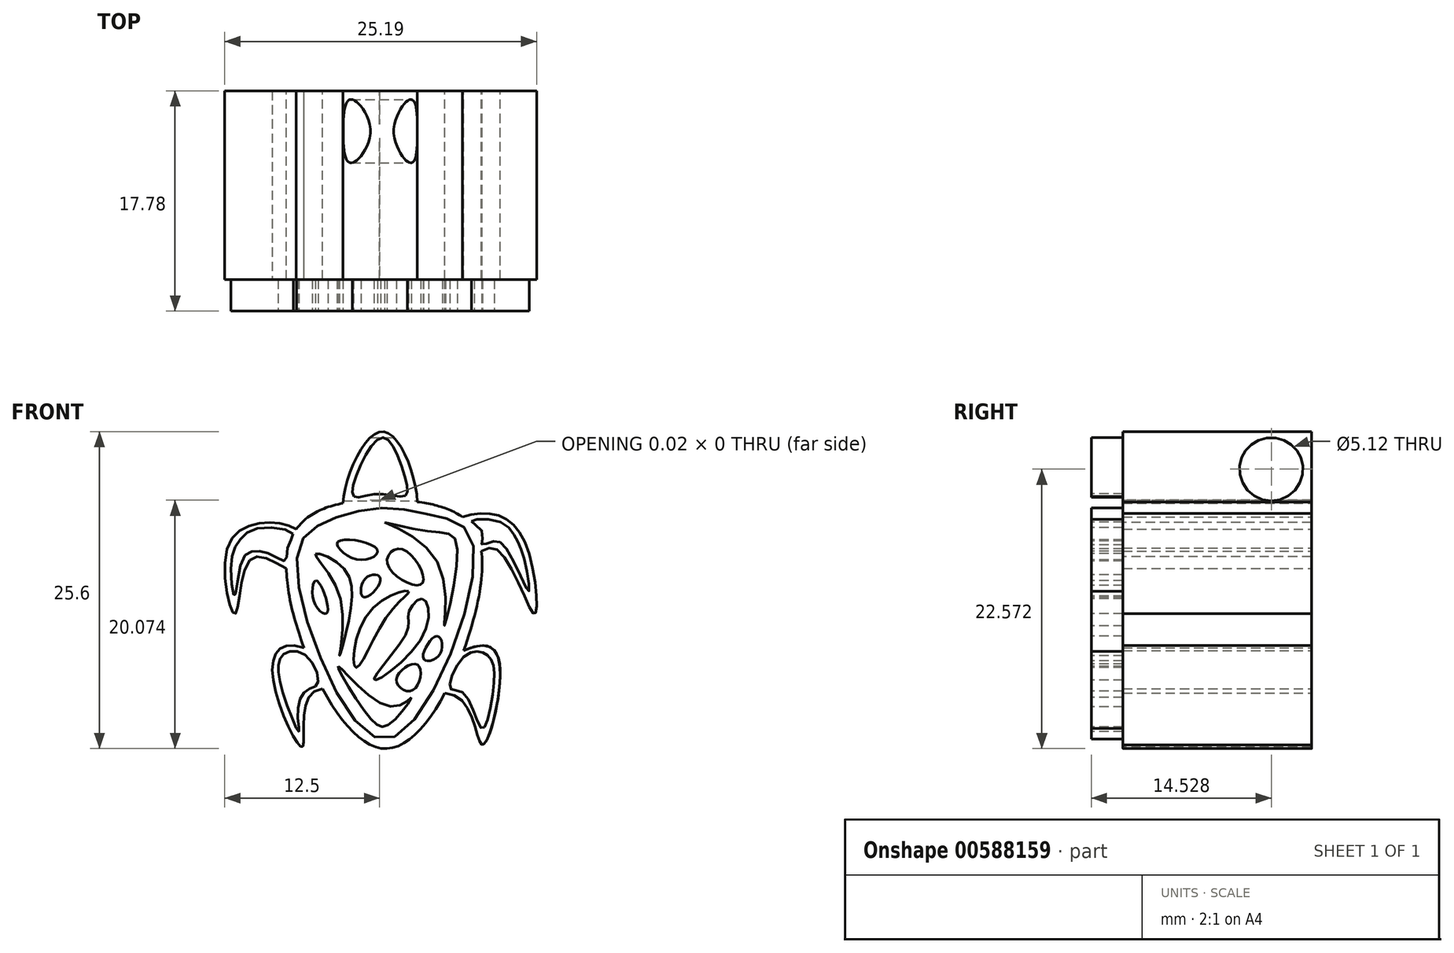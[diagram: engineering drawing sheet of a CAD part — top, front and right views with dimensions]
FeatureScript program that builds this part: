
annotation { "Feature Type Name" : "Feature", "Feature Type Description" : "" }
export const myFeature = defineFeature(function(context is Context, id is Id, definition is map)
    precondition{}
    {
        {
            var Q0;
            Q0=qCreatedBy(makeId("Front.planeOp"),FACE);
            var sketch = newSketch(context, id + "F0", { "sketchPlane" : qUnion([Q0])});
            skLineSegment(sketch, "E0.bottom", {"start": v(-20.81, 14.8) * mm, "end": v(4.78, 14.8) * mm});
            skLineSegment(sketch, "E0.top", {"start": v(-20.81, -10.8) * mm, "end": v(4.78, -10.8) * mm});
            skLineSegment(sketch, "E0.left", {"start": v(-20.81, 14.8) * mm, "end": v(-20.81, -10.8) * mm});
            skLineSegment(sketch, "E0.right", {"start": v(4.78, 14.8) * mm, "end": v(4.78, -10.8) * mm});
            skSolve(sketch);
        }
        {
            var Q0;
            Q0=qCreatedBy(makeId("Front.planeOp"),FACE);
            var sketch = newSketch(context, id + "F1", { "sketchPlane" : qUnion([Q0])});
            skFitSpline(sketch, "E1", {"points": [v(-7.9, 9.17) * mm, v(-2.14, 8.16) * mm, v(0, 3.25) * mm, v(-7.72, -10.9) * mm, v(-15.76, 2.93) * mm, v(-13.47, 8.16) * mm, v(-7.9, 9.17) * mm]});
            skSolve(sketch);
        }
        {
            var Q0;
            Q0 = qSketchRegion(id + "F1", true);
            extrude(context, id + "F2", {"entities" : qUnion([Q0]), "depth" : 25.4 * mm, "offsetDistance" : 25.4 * mm});
        }
        {
            var Q0;
            Q0=qCreatedBy(makeId("Front.planeOp"),FACE);
            var sketch = newSketch(context, id + "F3", { "sketchPlane" : qUnion([Q0])});
            skFitSpline(sketch, "E2", {"points": [v(-8.27, 9.17) * mm, v(-9, 7.94) * mm, v(-11.07, 7.83) * mm, v(-8.02, 14.7) * mm, v(-5.4, 7.61) * mm, v(-7.48, 7.83) * mm, v(-8.27, 9.17) * mm]});
            skSolve(sketch);
        }
        {
            var Q0;
            Q0 = qSketchRegion(id + "F3", true);
            extrude(context, id + "F4", {"entities" : qUnion([Q0]), "operationType" : NewBodyOperationType.ADD, "depth" : 25.4 * mm, "offsetDistance" : 25.4 * mm});
        }
        {
            var Q0;
            Q0=qCreatedBy(makeId("Front.planeOp"),FACE);
            var sketch = newSketch(context, id + "F5", { "sketchPlane" : qUnion([Q0])});
            skFitSpline(sketch, "E3", {"points": [v(-2.31, 7.52) * mm, v(1.17, 7.98) * mm, v(3.83, 4.78) * mm, v(4.2, 0) * mm, v(1.08, 5.23) * mm, v(-1.67, 4.23) * mm, v(-3.32, 6.15) * mm, v(-2.31, 7.52) * mm]});
            skFitSpline(sketch, "E4", {"points": [v(-14.23, 5.87) * mm, v(-16.8, 7.34) * mm, v(-20.55, 5.33) * mm, v(-19.91, 0) * mm, v(-18.54, 4.5) * mm, v(-14.78, 3.4) * mm, v(-14.23, 5.87) * mm]});
            skSolve(sketch);
        }
        {
            var Q0;
            Q0 = qSketchRegion(id + "F5", true);
            extrude(context, id + "F6", {"entities" : qUnion([Q0]), "operationType" : NewBodyOperationType.ADD, "depth" : 25.4 * mm, "offsetDistance" : 25.4 * mm});
        }
        {
            var Q0;
            Q0=makeQuery(id+"F0.imprint","IMPRINT",FACE,{"disambiguationData":[TD([[makeQuery(id+"F0.imprint","IMPRINT",EDGE,{"derivedFrom":sQuery(id+"F0.wireOp",EDGE,"E0.bottom")}),-1.0]])]});
            var sketch = newSketch(context, id + "F7", { "sketchPlane" : qUnion([Q0])});
            skFitSpline(sketch, "E5", {"points": [v(-15.18, -2.57) * mm, v(-16.88, -5.2) * mm, v(-14.5, -10.74) * mm, v(-13.72, -6.43) * mm, v(-9.79, -6.04) * mm, v(-15.18, -2.57) * mm]});
            skFitSpline(sketch, "E6", {"points": [v(0, -2.57) * mm, v(1.44, -5.72) * mm, v(0, -10.59) * mm, v(-1.9, -6.8) * mm, v(-5.65, -6.16) * mm, v(0, -2.57) * mm]});
            skSolve(sketch);
        }
        {
            var Q0;
            Q0 = qSketchRegion(id + "F7", true);
            extrude(context, id + "F8", {"entities" : qUnion([Q0]), "operationType" : NewBodyOperationType.ADD, "depth" : 25.4 * mm, "offsetDistance" : 25.4 * mm});
        }
        {
            var Q0;
            Q0=makeQuery(id+"F8.boolean.opBoolean","MERGE",FACE,{"derivedFrom":[makeQuery(id+"F6.boolean.opBoolean","MERGE",FACE,{"derivedFrom":[makeQuery(id+"F4.boolean.opBoolean","MERGE",FACE,{"derivedFrom":[makeQuery(id+"F2.opExtrude","CAP_FACE",FACE,{"disambiguationData":[OSD([sQuery(id+"F1.wireOp",EDGE,"E1")])],"isStart":false}),makeQuery(id+"F4.opExtrude","CAP_FACE",FACE,{"disambiguationData":[OSD([sQuery(id+"F3.wireOp",EDGE,"E2")])],"isStart":false})]}),makeQuery(id+"F6.opExtrude","CAP_FACE",FACE,{"disambiguationData":[OSD([sQuery(id+"F5.wireOp",EDGE,"E3")])],"isStart":false}),makeQuery(id+"F6.opExtrude","CAP_FACE",FACE,{"disambiguationData":[OSD([sQuery(id+"F5.wireOp",EDGE,"E4")])],"isStart":false})]}),makeQuery(id+"F8.opExtrude","CAP_FACE",FACE,{"disambiguationData":[OSD([sQuery(id+"F7.wireOp",EDGE,"E5")])],"isStart":false}),makeQuery(id+"F8.opExtrude","CAP_FACE",FACE,{"disambiguationData":[OSD([sQuery(id+"F7.wireOp",EDGE,"E6")])],"isStart":false})]});
            extrude(context, id + "F9", {"entities" : qUnion([Q0]), "operationType" : NewBodyOperationType.REMOVE, "oppositeDirection" : true, "depth" : 10.16 * mm, "offsetDistance" : 25.4 * mm});
        }
        {
            var Q0;
            Q0=makeQuery(id+"F0.imprint","IMPRINT",FACE,{"disambiguationData":[TD([[makeQuery(id+"F0.imprint","IMPRINT",EDGE,{"derivedFrom":sQuery(id+"F0.wireOp",EDGE,"E0.bottom")}),-1.0]])]});
            var sketch = newSketch(context, id + "F10", { "sketchPlane" : qUnion([Q0])});
            skFitSpline(sketch, "E7", {"points": [v(-8.1, 8.53) * mm, v(-12.56, 7.45) * mm, v(-14.8, 5.3) * mm, v(-12.87, -3.96) * mm, v(-8.02, -10.13) * mm, v(-3.08, -4.5) * mm, v(-0.92, 6.3) * mm, v(-3.78, 7.91) * mm, v(-8.1, 8.53) * mm]});
            skSolve(sketch);
        }
        {
            var Q0;
            Q0 = qSketchRegion(id + "F10", true);
            extrude(context, id + "F11", {"entities" : qUnion([Q0]), "operationType" : NewBodyOperationType.ADD, "depth" : 17.78 * mm, "offsetDistance" : 25.4 * mm});
        }
        {
            var Q0;
            Q0=makeQuery(id+"F0.imprint","IMPRINT",FACE,{"disambiguationData":[TD([[makeQuery(id+"F0.imprint","IMPRINT",EDGE,{"derivedFrom":sQuery(id+"F0.wireOp",EDGE,"E0.bottom")}),-1.0]])]});
            var sketch = newSketch(context, id + "F12", { "sketchPlane" : qUnion([Q0])});
            skFitSpline(sketch, "E8", {"points": [v(-10.33, 9.45) * mm, v(-8.4, 9.68) * mm, v(-6.17, 9.53) * mm, v(-6.4, 11.61) * mm, v(-7.94, 14.23) * mm, v(-9.87, 11.84) * mm, v(-10.33, 9.45) * mm]});
            skSolve(sketch);
        }
        {
            var Q0;
            Q0 = qSketchRegion(id + "F12", true);
            extrude(context, id + "F13", {"entities" : qUnion([Q0]), "operationType" : NewBodyOperationType.ADD, "depth" : 17.78 * mm, "offsetDistance" : 25.4 * mm});
        }
        {
            var Q0;
            Q0=makeQuery(id+"F0.imprint","IMPRINT",FACE,{"disambiguationData":[TD([[makeQuery(id+"F0.imprint","IMPRINT",EDGE,{"derivedFrom":sQuery(id+"F0.wireOp",EDGE,"E0.bottom")}),-1.0]])]});
            var sketch = newSketch(context, id + "F14", { "sketchPlane" : qUnion([Q0])});
            skFitSpline(sketch, "E9", {"points": [v(-15.26, 6.45) * mm, v(-15.65, 5.52) * mm, v(-15.88, 4.29) * mm, v(-16.96, 4.75) * mm, v(-18.35, 5.06) * mm, v(-19.35, 4.37) * mm, v(-19.96, 1.44) * mm, v(-20.27, 3.83) * mm, v(-19.66, 5.83) * mm, v(-18.04, 6.9) * mm, v(-15.26, 6.45) * mm]});
            skSolve(sketch);
        }
        {
            var Q0;
            Q0 = qSketchRegion(id + "F14", true);
            extrude(context, id + "F15", {"entities" : qUnion([Q0]), "operationType" : NewBodyOperationType.ADD, "depth" : 17.78 * mm, "offsetDistance" : 25.4 * mm});
        }
        {
            var Q0;
            Q0=makeQuery(id+"F0.imprint","IMPRINT",FACE,{"disambiguationData":[TD([[makeQuery(id+"F0.imprint","IMPRINT",EDGE,{"derivedFrom":sQuery(id+"F0.wireOp",EDGE,"E0.bottom")}),-1.0]])]});
            var sketch = newSketch(context, id + "F16", { "sketchPlane" : qUnion([Q0])});
            skFitSpline(sketch, "E10", {"points": [v(-0.85, 7.45) * mm, v(0, 6.68) * mm, v(0, 5.6) * mm, v(0.85, 5.83) * mm, v(2, 5.21) * mm, v(3.78, 1.82) * mm, v(3.47, 4.21) * mm, v(2.77, 6.06) * mm, v(1.39, 7.45) * mm, v(-0.85, 7.45) * mm]});
            skFitSpline(sketch, "E11", {"points": [v(-14.26, -3.34) * mm, v(-13.26, -5.65) * mm, v(-14.18, -6.2) * mm, v(-14.88, -7.97) * mm, v(-14.8, -9.5) * mm, v(-16.03, -6.5) * mm, v(-16.42, -4.04) * mm, v(-15.88, -3.19) * mm, v(-14.26, -3.34) * mm]});
            skSolve(sketch);
        }
        {
            var Q0;
            Q0 = qSketchRegion(id + "F16", true);
            extrude(context, id + "F17", {"entities" : qUnion([Q0]), "operationType" : NewBodyOperationType.ADD, "depth" : 17.78 * mm, "offsetDistance" : 25.4 * mm});
        }
        {
            var Q0;
            Q0=makeQuery(id+"F0.imprint","IMPRINT",FACE,{"disambiguationData":[TD([[makeQuery(id+"F0.imprint","IMPRINT",EDGE,{"derivedFrom":sQuery(id+"F0.wireOp",EDGE,"E0.bottom")}),-1.0]])]});
            var sketch = newSketch(context, id + "F18", { "sketchPlane" : qUnion([Q0])});
            skFitSpline(sketch, "E12", {"points": [v(-1.46, -3.5) * mm, v(-2.54, -6.04) * mm, v(-1.46, -6.43) * mm, v(0, -9.28) * mm, v(0.92, -6.12) * mm, v(0.77, -3.73) * mm, v(0, -3.11) * mm, v(-1.46, -3.5) * mm]});
            skSolve(sketch);
        }
        {
            var Q0;
            Q0 = qSketchRegion(id + "F18", true);
            extrude(context, id + "F19", {"entities" : qUnion([Q0]), "operationType" : NewBodyOperationType.ADD, "depth" : 17.78 * mm, "offsetDistance" : 25.4 * mm});
        }
        {
            var Q0;
            Q0=qCreatedBy(makeId("Right.planeOp"),FACE);
            var sketch = newSketch(context, id + "F20", { "sketchPlane" : qUnion([Q0])});
            skCircle(sketch, "E13", {"center": v(-3.25, 11.67) * mm, "radius": 2.56 * mm});
            skSolve(sketch);
        }
        {
            var Q0;
            Q0 = qSketchRegion(id + "F20", true);
            extrude(context, id + "F21", {"entities" : qUnion([Q0]), "operationType" : NewBodyOperationType.REMOVE, "oppositeDirection" : true, "depth" : 25.4 * mm, "offsetDistance" : 25.4 * mm});
        }
        {
            var Q0;
            Q0=qCreatedBy(makeId("Front.planeOp"),FACE);
            var sketch = newSketch(context, id + "F22", { "sketchPlane" : qUnion([Q0])});
            skFitSpline(sketch, "E14", {"points": [v(-5.65, -1.95) * mm, v(-3.76, 0.96) * mm, v(-3.6, 3.35) * mm, v(-2.74, 2.24) * mm, v(-2.65, 0) * mm, v(-1.88, 2.24) * mm, v(-3.08, 4.21) * mm, v(-1.54, 3.78) * mm, v(-0.94, 2.58) * mm, v(-0.77, 4.13) * mm, v(-3.5, 5.4) * mm, v(-4.28, 6.86) * mm, v(-5.82, 7.3) * mm, v(-4.88, 6.35) * mm, v(-4.53, 4.98) * mm, v(-5.48, 5.75) * mm, v(-6.59, 5.67) * mm, v(-5.73, 5.24) * mm, v(-4.7, 3.95) * mm, v(-5.99, 4.13) * mm, v(-7.36, 2.84) * mm, v(-6.25, 3.18) * mm, v(-4.88, 3.18) * mm, v(-4.88, 0.87) * mm, v(-7.36, -1.95) * mm, v(-6.76, -2.3) * mm, v(-5.65, -1.95) * mm]});
            skSolve(sketch);
        }
        {
            var Q0;
            Q0 = qSketchRegion(id + "F22", true);
            extrude(context, id + "F23", {"entities" : qUnion([Q0]), "operationType" : NewBodyOperationType.ADD, "depth" : 2.54 * mm, "offsetDistance" : 25.4 * mm});
        }
        {
            var Q0;
            Q0=makeQuery(id+"F11.opExtrude","CAP_FACE",FACE,{"disambiguationData":[OSD([sQuery(id+"F10.wireOp",EDGE,"E7")])],"isStart":false});
            var sketch = newSketch(context, id + "F24", { "sketchPlane" : qUnion([Q0])});
            skFitSpline(sketch, "E15", {"points": [v(-8.2, 2.85) * mm, v(-9.41, 2.85) * mm, v(-9.52, 1.33) * mm, v(-8.2, 2.85) * mm]});
            skSolve(sketch);
        }
        {
            var Q0;
            Q0 = qSketchRegion(id + "F24", true);
            extrude(context, id + "F25", {"entities" : qUnion([Q0]), "operationType" : NewBodyOperationType.REMOVE, "oppositeDirection" : true, "depth" : 2.54 * mm, "offsetDistance" : 25.4 * mm});
        }
        {
            var Q0;
            Q0=makeQuery(id+"F11.opExtrude","CAP_FACE",FACE,{"disambiguationData":[OSD([sQuery(id+"F10.wireOp",EDGE,"E7")])],"isStart":false});
            var sketch = newSketch(context, id + "F26", { "sketchPlane" : qUnion([Q0])});
            skFitSpline(sketch, "E16", {"points": [v(-7.87, 7.38) * mm, v(-4.24, 6.66) * mm, v(-2.06, 5.69) * mm, v(-3.03, -0.97) * mm, v(-3.63, 4.24) * mm, v(-7.87, 7.38) * mm]});
            skSolve(sketch);
        }
        {
            var Q0;
            Q0 = qSketchRegion(id + "F26", true);
            extrude(context, id + "F27", {"entities" : qUnion([Q0]), "operationType" : NewBodyOperationType.REMOVE, "oppositeDirection" : true, "depth" : 2.54 * mm, "offsetDistance" : 25.4 * mm});
        }
        {
            var Q0;
            Q0=makeQuery(id+"F11.opExtrude","CAP_FACE",FACE,{"disambiguationData":[OSD([sQuery(id+"F10.wireOp",EDGE,"E7")])],"isStart":false});
            var sketch = newSketch(context, id + "F28", { "sketchPlane" : qUnion([Q0])});
            skFitSpline(sketch, "E17", {"points": [v(-8.47, 5.2) * mm, v(-9.93, 4.36) * mm, v(-11.62, 5.81) * mm, v(-8.47, 5.2) * mm]});
            skSolve(sketch);
        }
        {
            var Q0;
            Q0 = qSketchRegion(id + "F28", true);
            extrude(context, id + "F29", {"entities" : qUnion([Q0]), "operationType" : NewBodyOperationType.REMOVE, "oppositeDirection" : true, "depth" : 2.54 * mm, "offsetDistance" : 25.4 * mm});
        }
        {
            var Q0;
            Q0=makeQuery(id+"F11.opExtrude","CAP_FACE",FACE,{"disambiguationData":[OSD([sQuery(id+"F10.wireOp",EDGE,"E7")])],"isStart":false});
            var sketch = newSketch(context, id + "F30", { "sketchPlane" : qUnion([Q0])});
            skFitSpline(sketch, "E18", {"points": [v(-11.62, -4.24) * mm, v(-9.2, -8.23) * mm, v(-7.5, -8.96) * mm, v(-5.69, -6.78) * mm, v(-7.38, -7.5) * mm, v(-11.62, -4.24) * mm]});
            skSolve(sketch);
        }
        {
            var Q0;
            Q0 = qSketchRegion(id + "F30", true);
            extrude(context, id + "F31", {"entities" : qUnion([Q0]), "operationType" : NewBodyOperationType.REMOVE, "oppositeDirection" : true, "depth" : 2.54 * mm, "offsetDistance" : 25.4 * mm});
        }
        {
            var Q0;
            Q0=makeQuery(id+"F11.opExtrude","CAP_FACE",FACE,{"disambiguationData":[OSD([sQuery(id+"F10.wireOp",EDGE,"E7")])],"isStart":false});
            var sketch = newSketch(context, id + "F32", { "sketchPlane" : qUnion([Q0])});
            skFitSpline(sketch, "E19", {"points": [v(-13.44, 4.84) * mm, v(-11.26, 3.75) * mm, v(-10.65, 0) * mm, v(-11.5, -3.39) * mm, v(-11.5, 1.45) * mm, v(-13.44, 4.84) * mm]});
            skSolve(sketch);
        }
        {
            var Q0;
            Q0 = qSketchRegion(id + "F32", true);
            extrude(context, id + "F33", {"entities" : qUnion([Q0]), "operationType" : NewBodyOperationType.REMOVE, "oppositeDirection" : true, "depth" : 2.54 * mm, "offsetDistance" : 25.4 * mm});
        }
        {
            var Q0;
            Q0=makeQuery(id+"F11.opExtrude","CAP_FACE",FACE,{"disambiguationData":[OSD([sQuery(id+"F10.wireOp",EDGE,"E7")])],"isStart":false});
            var sketch = newSketch(context, id + "F34", { "sketchPlane" : qUnion([Q0])});
            skFitSpline(sketch, "E20", {"points": [v(-13.44, 2.66) * mm, v(-12.59, 1.21) * mm, v(-12.59, 0) * mm, v(-13.56, 0.97) * mm, v(-13.44, 2.66) * mm]});
            skSolve(sketch);
        }
        {
            var Q0;
            Q0 = qSketchRegion(id + "F34", true);
            extrude(context, id + "F35", {"entities" : qUnion([Q0]), "operationType" : NewBodyOperationType.REMOVE, "oppositeDirection" : true, "depth" : 2.54 * mm, "offsetDistance" : 25.4 * mm});
        }
        {
            var Q0;
            Q0=makeQuery(id+"F11.opExtrude","CAP_FACE",FACE,{"disambiguationData":[OSD([sQuery(id+"F10.wireOp",EDGE,"E7")])],"isStart":false});
            var sketch = newSketch(context, id + "F36", { "sketchPlane" : qUnion([Q0])});
            skFitSpline(sketch, "E21", {"points": [v(-5.93, 1.82) * mm, v(-9.2, 0) * mm, v(-10.17, -4.36) * mm, v(-7.5, 0) * mm, v(-5.93, 1.82) * mm]});
            skSolve(sketch);
        }
        {
            var Q0;
            Q0 = qSketchRegion(id + "F36", true);
            extrude(context, id + "F37", {"entities" : qUnion([Q0]), "operationType" : NewBodyOperationType.REMOVE, "oppositeDirection" : true, "depth" : 2.54 * mm, "offsetDistance" : 25.4 * mm});
        }
        {
            var Q0;
            Q0=makeQuery(id+"F11.opExtrude","CAP_FACE",FACE,{"disambiguationData":[OSD([sQuery(id+"F10.wireOp",EDGE,"E7")])],"isStart":false});
            var sketch = newSketch(context, id + "F38", { "sketchPlane" : qUnion([Q0])});
            skFitSpline(sketch, "E22", {"points": [v(-6.42, 5.2) * mm, v(-7.63, 4) * mm, v(-4.84, 2.42) * mm, v(-6.42, 5.2) * mm]});
            skSolve(sketch);
        }
        {
            var Q0;
            Q0 = qSketchRegion(id + "F38", true);
            extrude(context, id + "F39", {"entities" : qUnion([Q0]), "operationType" : NewBodyOperationType.REMOVE, "oppositeDirection" : true, "depth" : 2.54 * mm, "offsetDistance" : 25.4 * mm});
        }
        {
            var Q0;
            Q0=makeQuery(id+"F11.opExtrude","CAP_FACE",FACE,{"disambiguationData":[OSD([sQuery(id+"F10.wireOp",EDGE,"E7")])],"isStart":false});
            var sketch = newSketch(context, id + "F40", { "sketchPlane" : qUnion([Q0])});
            skFitSpline(sketch, "E23", {"points": [v(-4.84, 1.21) * mm, v(-4.72, -1.7) * mm, v(-8.72, -5.33) * mm, v(-6.05, -1.45) * mm, v(-5.93, 0) * mm, v(-4.84, 1.21) * mm]});
            skSolve(sketch);
        }
        {
            var Q0;
            Q0 = qSketchRegion(id + "F40", true);
            extrude(context, id + "F41", {"entities" : qUnion([Q0]), "operationType" : NewBodyOperationType.REMOVE, "oppositeDirection" : true, "depth" : 2.54 * mm, "offsetDistance" : 25.4 * mm});
        }
        {
            var Q0;
            Q0=makeQuery(id+"F11.opExtrude","CAP_FACE",FACE,{"disambiguationData":[OSD([sQuery(id+"F10.wireOp",EDGE,"E7")])],"isStart":false});
            var sketch = newSketch(context, id + "F42", { "sketchPlane" : qUnion([Q0])});
            skFitSpline(sketch, "E24", {"points": [v(-5.2, -4.12) * mm, v(-6.9, -5.33) * mm, v(-5.57, -6.17) * mm, v(-5.2, -4.12) * mm]});
            skSolve(sketch);
        }
        {
            var Q0;
            Q0 = qSketchRegion(id + "F42", true);
            extrude(context, id + "F43", {"entities" : qUnion([Q0]), "operationType" : NewBodyOperationType.REMOVE, "oppositeDirection" : true, "depth" : 2.54 * mm, "offsetDistance" : 25.4 * mm});
        }
        {
            var Q0;
            Q0=makeQuery(id+"F11.opExtrude","CAP_FACE",FACE,{"disambiguationData":[OSD([sQuery(id+"F10.wireOp",EDGE,"E7")])],"isStart":false});
            var sketch = newSketch(context, id + "F44", { "sketchPlane" : qUnion([Q0])});
            skSolve(sketch);
        }
        {
            var Q0;
            Q0=makeQuery(id+"F44.imprint","IMPRINT",FACE,{"disambiguationData":[TD([[makeQuery(id+"F44.imprint","IMPRINT",EDGE,{"derivedFrom":makeQuery(id+"F11.opExtrude","CAP_EDGE",EDGE,{"disambiguationData":[OSD([sQuery(id+"F10.wireOp",EDGE,"E7")])],"isStart":false})}),1.0]])]});
            var sketch = newSketch(context, id + "F45", { "sketchPlane" : qUnion([Q0])});
            skFitSpline(sketch, "E25", {"points": [v(-3.63, -1.82) * mm, v(-4.72, -3.63) * mm, v(-3.39, -3.27) * mm, v(-3.63, -1.82) * mm]});
            skSolve(sketch);
        }
        {
            var Q0;
            Q0 = qSketchRegion(id + "F45", true);
            extrude(context, id + "F46", {"entities" : qUnion([Q0]), "operationType" : NewBodyOperationType.REMOVE, "oppositeDirection" : true, "depth" : 2.54 * mm, "offsetDistance" : 25.4 * mm});
        }
    });
